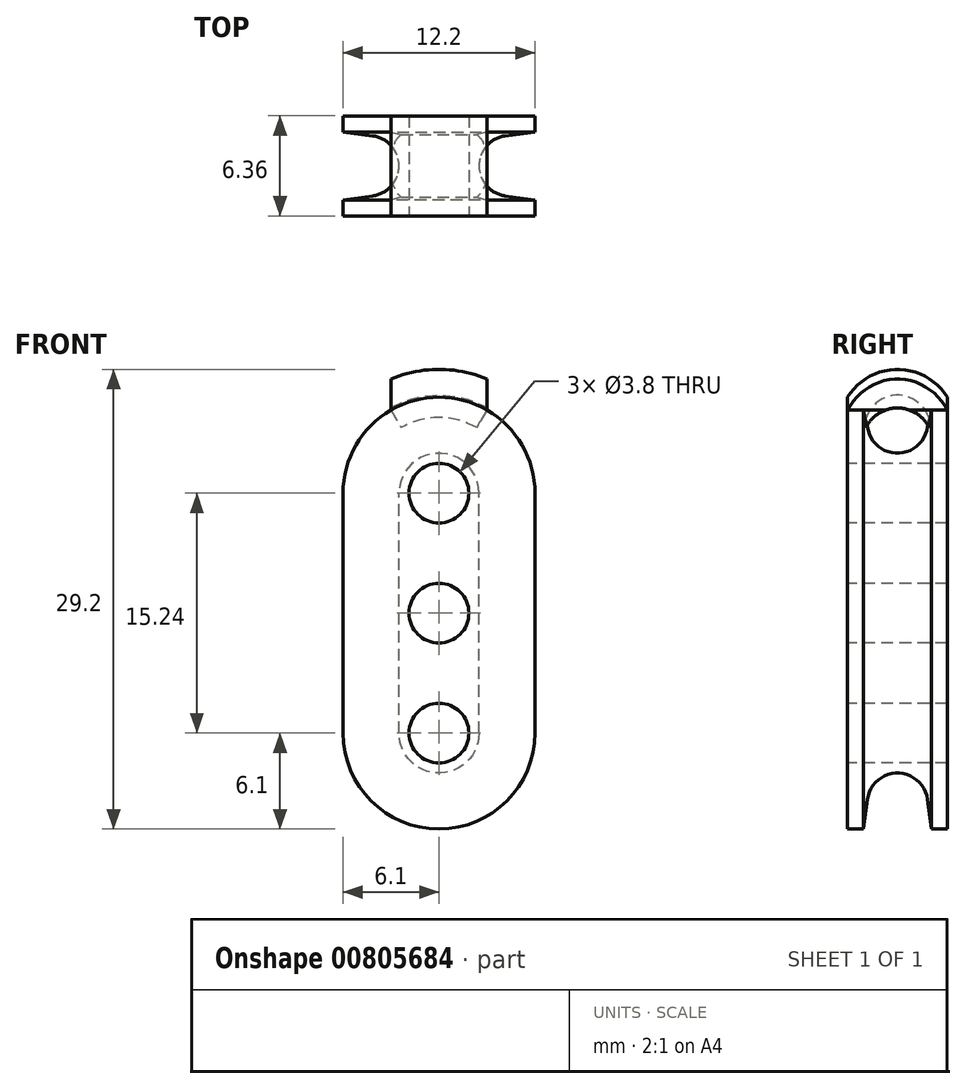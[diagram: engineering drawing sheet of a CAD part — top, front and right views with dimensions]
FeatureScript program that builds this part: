
annotation { "Feature Type Name" : "Feature", "Feature Type Description" : "" }
export const myFeature = defineFeature(function(context is Context, id is Id, definition is map)
    precondition{}
    {
        {
            var Q0;
            Q0=qCreatedBy(makeId("Front.planeOp"),FACE);
            var sketch = newSketch(context, id + "F0", { "sketchPlane" : qUnion([Q0])});
            skCircle(sketch, "E0", {"center": v(0, 0) * mm, "radius": 6.1 * mm});
            skSolve(sketch);
        }
        {
            var Q0;
            Q0=makeQuery(id+"F0.imprint","IMPRINT",FACE,{"disambiguationData":[TD([[makeQuery(id+"F0.imprint","IMPRINT",EDGE,{"derivedFrom":sQuery(id+"F0.wireOp",EDGE,"E0")}),1.0]])]});
            extrude(context, id + "F1", {"entities" : qUnion([Q0]), "depth" : 6.35 * mm, "offsetDistance" : 25.4 * mm, "symmetric" : true});
        }
        {
            var Q0;
            Q0=qCreatedBy(makeId("Front.planeOp"),FACE);
            var sketch = newSketch(context, id + "F2", { "sketchPlane" : qUnion([Q0])});
            skLineSegment(sketch, "E1.bottom", {"start": v(12.6, 0) * mm, "end": v(-13.53, 0) * mm});
            skLineSegment(sketch, "E1.top", {"start": v(12.6, -24.15) * mm, "end": v(-13.53, -24.15) * mm});
            skLineSegment(sketch, "E1.left", {"start": v(12.6, 0) * mm, "end": v(12.6, -24.15) * mm});
            skLineSegment(sketch, "E1.right", {"start": v(-13.53, 0) * mm, "end": v(-13.53, -24.15) * mm});
            skSolve(sketch);
        }
        {
            var Q0;
            Q0=qSketchRegion(id+"F2",true);
            extrude(context, id + "F3", {"entities" : qUnion([Q0]), "operationType" : NewBodyOperationType.REMOVE, "oppositeDirection" : true, "depth" : 25.4 * mm, "offsetDistance" : 25.4 * mm, "symmetric" : true});
        }
        {
            var Q0;
            Q0=makeQuery(id+"F1.opExtrude","CAP_FACE",FACE,{"disambiguationData":[OSD([sQuery(id+"F0.wireOp",EDGE,"E0")])],"isStart":false});
            var sketch = newSketch(context, id + "F4", { "sketchPlane" : qUnion([Q0])});
            skCircle(sketch, "E2", {"center": v(0, 0) * mm, "radius": 1.9 * mm});
            skSolve(sketch);
        }
        {
            var Q0;
            {var subQ0=makeQuery(id+"F8.boolean.opBoolean","MERGE",FACE,{"derivedFrom":[makeQuery(id+"F1.opExtrude","CAP_FACE",FACE,{"disambiguationData":[OSD([sQuery(id+"F0.wireOp",EDGE,"E0")])],"isStart":false}),makeQuery(id+"F8.opExtrude","SWEPT_FACE",FACE,{"disambiguationData":[OSD([sQuery(id+"FHCKBcZkIibrD3C_1.wireOp",EDGE,"33893b92-1531-43ea-a95e-b28fcb7d8d0e.6")])]})]});Q0=makeQuery(id+"F9.boolean.opBoolean","MERGE",FACE,{"derivedFrom":[subQ0,makeQuery(id+"F9.opPattern","COPY",FACE,{"derivedFrom":subQ0,"instanceName":"1"})]});}
            extrude(context, id + "F5", {"entities" : qUnion([Q0]), "operationType" : NewBodyOperationType.ADD, "depth" : 3.17 * mm - 1.02 * mm, "offsetDistance" : 25.4 * mm});
        }
        {
            var Q0;
            Q0=qCreatedBy(makeId("Right.planeOp"),FACE);
            var sketch = newSketch(context, id + "F6", { "sketchPlane" : qUnion([Q0])});
            skLineSegment(sketch, "E3", {"start": v(2.41, 7.99) * mm, "end": v(1.9, 4.2) * mm});
            skLineSegment(sketch, "E4", {"start": v(-2.41, 7.99) * mm, "end": v(-1.9, 4.2) * mm});
            skLineSegment(sketch, "E5", {"start": v(2.41, 7.99) * mm, "end": v(-2.41, 7.99) * mm});
            skArc(sketch, "E6", {"start": v(-1.9, 4.2) * mm, "mid": v(0, 2.54) * mm, "end": v(1.9, 4.2) * mm});
            skLineSegment(sketch, "E7", {"start": v(11.1, 0) * mm, "end": v(0, 0) * mm, "construction": true});
            skPoint(sketch, "E8", {"position": v(0, 2.54) * mm});
            skLineSegment(sketch, "E9", {"start": v(0, 0) * mm, "end": v(0, 4.46) * mm, "construction": true});
            skLineSegment(sketch, "E10.0", {"start": v(3.18, 0) * mm, "end": v(3.18, 6.1) * mm, "construction": true});
            skPoint(sketch, "E11", {"position": v(2.16, 6.1) * mm});
            skPoint(sketch, "E12", {"position": v(-2.16, 6.1) * mm});
            skLineSegment(sketch, "E13.1.0.0", {"start": v(-2.92, 7.99) * mm, "end": v(-3.43, 4.2) * mm});
            skLineSegment(sketch, "E13.direction1", {"start": v(-1.9, 4.2) * mm, "end": v(-7.24, 4.2) * mm, "construction": true});
            skPoint(sketch, "E14", {"position": v(-3.18, 6.1) * mm});
            skLineSegment(sketch, "E15", {"start": v(2.16, 6.1) * mm, "end": v(3.18, 6.1) * mm, "construction": true});
            skLineSegment(sketch, "E16", {"start": v(-3.18, 6.1) * mm, "end": v(-2.16, 6.1) * mm, "construction": true});
            skArc(sketch, "E17", {"start": v(-3.43, 4.2) * mm, "mid": v(-3.68, 3.74) * mm, "end": v(-4.17, 3.56) * mm});
            skLineSegment(sketch, "E18", {"start": v(-4.17, 3.56) * mm, "end": v(-5.95, 3.56) * mm});
            skLineSegment(sketch, "E19", {"start": v(-5.95, 3.56) * mm, "end": v(-5.95, 7.99) * mm});
            skLineSegment(sketch, "E20", {"start": v(-5.95, 7.99) * mm, "end": v(-2.92, 7.99) * mm});
            skSolve(sketch);
        }
        {
            var Q0;
            Q0=makeQuery(id+"F6.imprint","IMPRINT",FACE,{"disambiguationData":[TD([[makeQuery(id+"F6.imprint","IMPRINT",EDGE,{"derivedFrom":sQuery(id+"F6.wireOp",EDGE,"E3")}),-1.0]])]});
            var Q1;
            Q1=makeQuery(id+"F6.imprint","IMPRINT",FACE,{"disambiguationData":[TD([[makeQuery(id+"F6.imprint","IMPRINT",EDGE,{"derivedFrom":sQuery(id+"F6.wireOp",EDGE,"E13.1.0.0")}),-1.0]])]});
            var Q2;
            Q2=sQuery(id+"F6.wireOp",EDGE,"E7");
            var Q3;
            Q3=sQuery(id+"F6.wireOp",EDGE,"E7");
            revolve(context, id + "F7", {"operationType" : NewBodyOperationType.REMOVE, "surfaceOperationType" : NewSurfaceOperationType.NEW, "entities" : qUnion([Q0, Q1]), "surfaceEntities" : qUnion([Q2]), "axis" : qUnion([Q3]), "revolveType" : RevolveType.FULL, "oppositeDirection" : true});
        }
        {
            var Q0;
            {var subQ0=sQuery(id+"F2.wireOp",EDGE,"E1.bottom");Q0=makeQuery(id+"F5.boolean.opBoolean","MERGE",FACE,{"derivedFrom":[makeQuery(id+"F3.boolean.opBoolean","COPY",FACE,{"derivedFrom":makeQuery(id+"F3.opExtrude","SWEPT_FACE",FACE,{"disambiguationData":[OSD([subQ0])]})}),makeQuery(id+"F5.opExtrude","SWEPT_FACE",FACE,{"disambiguationData":[OSD([sQuery(id+"F0.wireOp",EDGE,"E0"),subQ0])]})]});}
            extrude(context, id + "F8", {"entities" : qUnion([Q0]), "operationType" : NewBodyOperationType.ADD, "depth" : 7.62 * mm, "offsetDistance" : 25.4 * mm});
        }
        {
            var Q0;
            Q0=makeQuery(id+"F1.opExtrude","SWEPT_BODY",BODY,{"disambiguationData":[OSD([sQuery(id+"F0.wireOp",EDGE,"E0")])]});
            var Q1;
            Q1=makeQuery(id+"F8.opExtrude","CAP_FACE",FACE,{"disambiguationData":[OSD([sQuery(id+"F0.wireOp",EDGE,"E0"),sQuery(id+"F2.wireOp",EDGE,"E1.bottom")])],"isStart":false});
            mirror(context, id + "F9", {"operationType" : NewBodyOperationType.ADD, "entities" : qUnion([Q0]), "mirrorPlane" : qUnion([Q1])});
        }
        {
            var Q0;
            Q0=qSketchRegion(id+"F4",true);
            extrude(context, id + "F10", {"entities" : qUnion([Q0]), "operationType" : NewBodyOperationType.REMOVE, "oppositeDirection" : true, "depth" : 127 * mm, "offsetDistance" : 25.4 * mm, "symmetric" : true});
        }
        {
            var Q0;
            {var subQ0=sQuery(id+"F2.wireOp",EDGE,"E1.bottom");var subQ1=sQuery(id+"F0.wireOp",EDGE,"E0");var subQ2=makeQuery(id+"F8.boolean.opBoolean","MERGE",FACE,{"derivedFrom":[makeQuery(id+"F5.opExtrude","CAP_FACE",FACE,{"disambiguationData":[OSD([subQ1])],"isStart":false}),makeQuery(id+"F8.opExtrude","SWEPT_FACE",FACE,{"disambiguationData":[OSD([subQ1,subQ0]),TDD([makeQuery(id+"F5.opExtrude","CAP_EDGE",EDGE,{"disambiguationData":[OSD([subQ1,subQ0])],"isStart":false})])]})]});Q0=makeQuery(id+"F9.boolean.opBoolean","MERGE",FACE,{"derivedFrom":[subQ2,makeQuery(id+"F9.opPattern","COPY",FACE,{"derivedFrom":subQ2,"instanceName":"1"})]});}
            var sketch = newSketch(context, id + "F11", { "sketchPlane" : qUnion([Q0])});
            skCircle(sketch, "E21.0", {"center": v(0, 0) * mm, "radius": 1.9 * mm});
            skCircle(sketch, "E22.0.1.0", {"center": v(0, -7.62) * mm, "radius": 1.9 * mm});
            skCircle(sketch, "E22.0.2.0", {"center": v(0, -15.24) * mm, "radius": 1.9 * mm});
            skLineSegment(sketch, "E22.direction1", {"start": v(0, 0) * mm, "end": v(25.4, 0) * mm, "construction": true});
            skLineSegment(sketch, "E22.direction2", {"start": v(0, 0) * mm, "end": v(0, -7.62) * mm, "construction": true});
            skSolve(sketch);
        }
        {
            var Q0;
            Q0=makeQuery(id+"F11.imprint","IMPRINT",FACE,{"disambiguationData":[TD([[makeQuery(id+"F11.imprint","IMPRINT",EDGE,{"derivedFrom":sQuery(id+"F11.wireOp",EDGE,"E22.0.1.0")}),1.0]])]});
            var Q1;
            Q1=makeQuery(id+"F11.imprint","IMPRINT",FACE,{"disambiguationData":[TD([[makeQuery(id+"F11.imprint","IMPRINT",EDGE,{"derivedFrom":sQuery(id+"F11.wireOp",EDGE,"E22.0.2.0")}),1.0]])]});
            extrude(context, id + "F12", {"entities" : qUnion([Q0, Q1]), "operationType" : NewBodyOperationType.REMOVE, "endBound" : BoundingType.THROUGH_ALL, "oppositeDirection" : true, "depth" : 25.4 * mm, "offsetDistance" : 25.4 * mm});
        }
        {
            var Q0;
            Q0=qCreatedBy(makeId("Right.planeOp"),FACE);
            var sketch = newSketch(context, id + "F13", { "sketchPlane" : qUnion([Q0])});
            skLineSegment(sketch, "E23.bottom", {"start": v(-3.18, 10.31) * mm, "end": v(-10.8, 10.31) * mm});
            skLineSegment(sketch, "E23.top", {"start": v(-3.17, -24.1) * mm, "end": v(-10.8, -24.1) * mm});
            skLineSegment(sketch, "E23.left", {"start": v(-3.18, 10.31) * mm, "end": v(-3.17, -24.1) * mm});
            skLineSegment(sketch, "E23.right", {"start": v(-10.8, 10.31) * mm, "end": v(-10.8, -24.1) * mm});
            skSolve(sketch);
        }
        {
            var Q0;
            Q0=qSketchRegion(id+"F13",true);
            extrude(context, id + "F14", {"entities" : qUnion([Q0]), "operationType" : NewBodyOperationType.REMOVE, "depth" : 127 * mm, "offsetDistance" : 25.4 * mm, "symmetric" : true});
        }
        {
            var Q0;
            Q0=qCreatedBy(makeId("Right.planeOp"),FACE);
            var sketch = newSketch(context, id + "F15", { "sketchPlane" : qUnion([Q0])});
            skCircle(sketch, "E24", {"center": v(0, 4.13) * mm, "radius": 1.59 * mm, "construction": true});
            skArc(sketch, "E25", {"start": v(1.98, 4.8) * mm, "mid": v(0, 6.22) * mm, "end": v(-1.98, 4.8) * mm});
            skPoint(sketch, "E26", {"position": v(0, 6.22) * mm});
            skPoint(sketch, "E27", {"position": v(0, 5.72) * mm});
            skLineSegment(sketch, "E28", {"start": v(-1.98, 4.8) * mm, "end": v(-3.17, 4.8) * mm});
            skLineSegment(sketch, "E29", {"start": v(1.98, 4.8) * mm, "end": v(3.18, 4.8) * mm});
            skPoint(sketch, "E30.0", {"position": v(11.1, 0) * mm});
            skPoint(sketch, "E31.0", {"position": v(0, 0) * mm});
            skLineSegment(sketch, "E32.0", {"start": v(11.1, 0) * mm, "end": v(0, 0) * mm, "construction": true});
            skArc(sketch, "E33", {"start": v(3.17, 6.1) * mm, "mid": v(0, 7.86) * mm, "end": v(-3.17, 6.1) * mm});
            skLineSegment(sketch, "E34", {"start": v(-3.17, 6.1) * mm, "end": v(-3.17, 4.8) * mm});
            skLineSegment(sketch, "E35", {"start": v(3.17, 6.1) * mm, "end": v(3.18, 4.8) * mm});
            skSolve(sketch);
        }
        {
            var Q0;
            Q0 = qSketchRegion(id + "F15", true);
            var Q1;
            Q1=sQuery(id+"F15.wireOp",EDGE,"E32.0");
            revolve(context, id + "F16", {"operationType" : NewBodyOperationType.ADD, "surfaceOperationType" : NewSurfaceOperationType.NEW, "entities" : qUnion([Q0]), "axis" : qUnion([Q1]), "revolveType" : RevolveType.SYMMETRIC, "angle" : 60 * degree});
        }
        {
            var Q0;
            Q0=qCreatedBy(makeId("Front.planeOp"),FACE);
            var sketch = newSketch(context, id + "F17", { "sketchPlane" : qUnion([Q0])});
            skLineSegment(sketch, "E36.bottom", {"start": v(3.05, 5.28) * mm, "end": v(4.24, 5.28) * mm});
            skLineSegment(sketch, "E36.top", {"start": v(3.05, 11) * mm, "end": v(4.24, 11) * mm});
            skLineSegment(sketch, "E36.left", {"start": v(3.05, 5.28) * mm, "end": v(3.05, 11) * mm});
            skLineSegment(sketch, "E36.right", {"start": v(4.24, 5.28) * mm, "end": v(4.24, 11) * mm});
            skLineSegment(sketch, "E37", {"start": v(0, 0) * mm, "end": v(0, 10.43) * mm, "construction": true});
            skLineSegment(sketch, "E38.MirrorCS", {"start": v(-3.05, 5.28) * mm, "end": v(-3.05, 11) * mm});
            skLineSegment(sketch, "E39.MirrorCS", {"start": v(-3.05, 5.28) * mm, "end": v(-4.24, 5.28) * mm});
            skLineSegment(sketch, "E40.MirrorCS", {"start": v(-3.05, 11) * mm, "end": v(-4.24, 11) * mm});
            skLineSegment(sketch, "E41.MirrorCS", {"start": v(-4.24, 5.28) * mm, "end": v(-4.24, 11) * mm});
            skSolve(sketch);
        }
        {
            var Q0;
            Q0 = qSketchRegion(id + "F17", true);
            extrude(context, id + "F18", {"entities" : qUnion([Q0]), "operationType" : NewBodyOperationType.REMOVE, "oppositeDirection" : true, "depth" : 25.4 * mm, "offsetDistance" : 25.4 * mm, "symmetric" : true});
        }
    });
